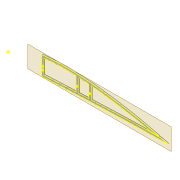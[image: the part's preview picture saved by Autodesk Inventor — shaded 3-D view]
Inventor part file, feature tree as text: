
AUTODESK INVENTOR PART (.ipt)
format: ipt  version: 2022 (Build 260153000, 153)  size: 363,008 bytes
history: native  units: mm
features: extrude x6, sketch x6, projected_geometry x5, shell x1, fillet x1, plane x1
ambient origin geometry x8: Origin, YZ Plane, XZ Plane, XY Plane, X Axis, Y Axis, Z Axis, Center Point
bodies: Solid1 (feature_tree)
feature tree (20):
  extrude  "Extrusion1"  Depth=4.0mm
  shell  "Shell1"  Thickness=5.0mm
  extrude  "Extrusion2"  Depth=2.0mm
  extrude  "Extrusion3"  Depth=5.9mm
  extrude  "Extrusion4"  Depth=10.0mm TaperAngle=0.0deg
  fillet  "Fillet1"  Radius=65.0mm
  extrude  "Extrusion5"  Depth=2.0mm TaperAngle=0.0deg
  plane  "Work Plane2"
  extrude  "Extrusion8"  Depth=1.0mm
  sketch  "Sketch17"  dims[d31=2.0mm d32=5.0mm d34=1.6mm d35=2.5mm d37=5.0mm d38=1.6mm d40=2.5mm d41=65.0mm d42=20.0mm d43=1.0mm d44=10.0mm d45=0.0mm d46=2.5mm d47=2.5mm]
  sketch  "Sketch3"  dims[d0=2.0mm d1=0.0mm d2=4.0mm d3=5.0mm]
  projected_geometry  "Projected Loop3"
  sketch  "Sketch8"  dims[d5=2.0mm d6=0.0mm d7=2.0mm]
  sketch  "Sketch9"  dims[d8=2.0mm d9=5.9mm]
  sketch  "Sketch10"  dims[d12=8.0mm d13=10.0mm d14=0.0mm d15=65.0mm]
  projected_geometry  "Projected Loop4"
  projected_geometry  "Projected Loop10"
  sketch  "Sketch16"  dims[d16=10.0mm d17=0.0mm d22=2.0mm d23=0.0mm]
  projected_geometry  "Projected Loop11"
  projected_geometry  "Project Cut Edges1"
